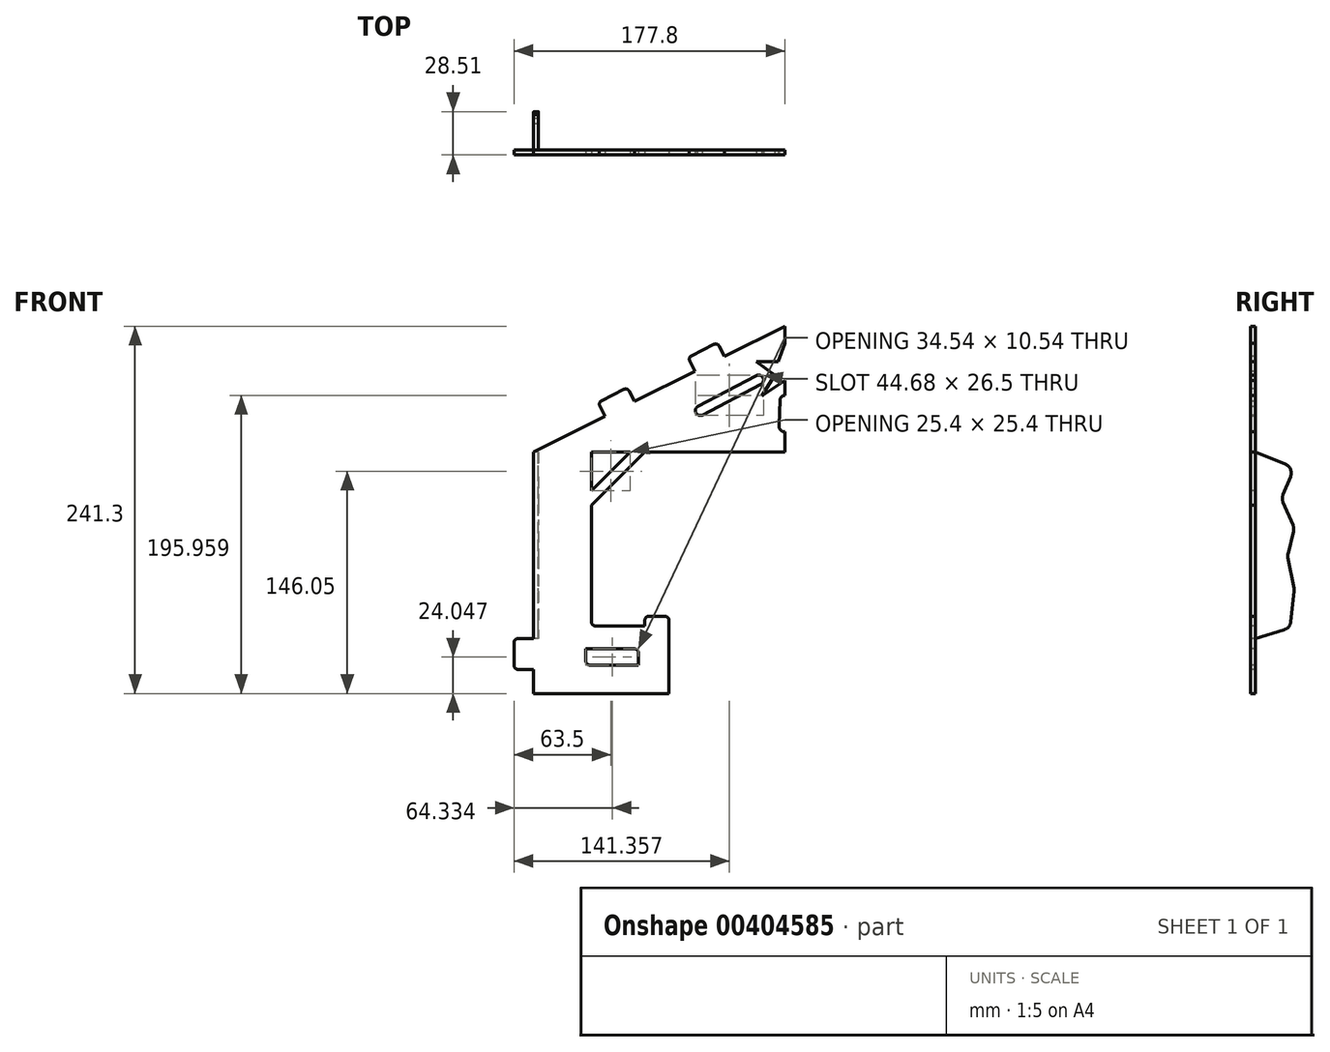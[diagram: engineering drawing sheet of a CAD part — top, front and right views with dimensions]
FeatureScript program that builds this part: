
annotation { "Feature Type Name" : "Feature", "Feature Type Description" : "" }
export const myFeature = defineFeature(function(context is Context, id is Id, definition is map)
    precondition{}
    {
        {
            var Q0;
            Q0=qCreatedBy(makeId("Front.planeOp"),FACE);
            var sketch = newSketch(context, id + "F0", { "sketchPlane" : qUnion([Q0])});
            skLineSegment(sketch, "E0", {"start": v(0, 0) * mm, "end": v(0, 82.55) * mm});
            skLineSegment(sketch, "E1", {"start": v(0, 0) * mm, "end": v(127, 0) * mm});
            skLineSegment(sketch, "E2", {"start": v(127, 0) * mm, "end": v(127, -114.3) * mm});
            skLineSegment(sketch, "E3", {"start": v(127, -114.3) * mm, "end": v(76.2, -114.3) * mm});
            skLineSegment(sketch, "E4", {"start": v(76.2, -114.3) * mm, "end": v(76.2, -158.75) * mm});
            skLineSegment(sketch, "E5", {"start": v(76.2, -158.75) * mm, "end": v(165.1, -158.75) * mm});
            skLineSegment(sketch, "E6", {"start": v(165.1, -158.75) * mm, "end": v(165.1, 0) * mm});
            skPoint(sketch, "E7.orphan", {"position": v(193.1, 0) * mm});
            skLineSegment(sketch, "E8", {"start": v(0, 82.55) * mm, "end": v(165.1, 0) * mm});
            skSolve(sketch);
        }
        {
            var Q0;
            Q0=makeQuery(id+"F0.imprint","IMPRINT",FACE,{"disambiguationData":[TD([[makeQuery(id+"F0.imprint","IMPRINT",EDGE,{"derivedFrom":sQuery(id+"F0.wireOp",EDGE,"E0")}),-1.0]])]});
            extrude(context, id + "F1", {"entities" : qUnion([Q0]), "oppositeDirection" : true, "depth" : 3.17 * mm});
        }
        {
            var Q0;
            Q0=makeQuery(id+"F1.opExtrude","CAP_FACE",FACE,{"disambiguationData":[OSD([sQuery(id+"F0.wireOp",EDGE,"E0"),sQuery(id+"F0.wireOp",EDGE,"E1"),sQuery(id+"F0.wireOp",EDGE,"E2"),sQuery(id+"F0.wireOp",EDGE,"E3"),sQuery(id+"F0.wireOp",EDGE,"E4"),sQuery(id+"F0.wireOp",EDGE,"E5"),sQuery(id+"F0.wireOp",EDGE,"E6"),sQuery(id+"F0.wireOp",EDGE,"E8")])],"isStart":true});
            var sketch = newSketch(context, id + "F2", { "sketchPlane" : qUnion([Q0])});
            skLineSegment(sketch, "E9", {"start": v(39.76, 62.67) * mm, "end": v(44.3, 71.76) * mm});
            skLineSegment(sketch, "E10", {"start": v(44.3, 71.76) * mm, "end": v(63.61, 62.1) * mm});
            skLineSegment(sketch, "E11", {"start": v(63.61, 62.1) * mm, "end": v(59.07, 53.02) * mm});
            skLineSegment(sketch, "E12", {"start": v(59.07, 53.02) * mm, "end": v(39.76, 62.67) * mm});
            skLineSegment(sketch, "E13", {"start": v(78.95, 43.08) * mm, "end": v(85.06, 55.3) * mm, "construction": true});
            skLineSegment(sketch, "E14.MirrorCS", {"start": v(103.37, 42.22) * mm, "end": v(98.83, 33.14) * mm});
            skLineSegment(sketch, "E15.MirrorCS", {"start": v(122.68, 32.57) * mm, "end": v(103.37, 42.22) * mm});
            skLineSegment(sketch, "E16.MirrorCS", {"start": v(118.14, 23.48) * mm, "end": v(122.68, 32.57) * mm});
            skLineSegment(sketch, "E17.MirrorCS", {"start": v(98.83, 33.14) * mm, "end": v(118.14, 23.48) * mm});
            skLineSegment(sketch, "E18.bottom", {"start": v(76.2, -114.3) * mm, "end": v(91.95, -114.3) * mm});
            skLineSegment(sketch, "E18.top", {"start": v(76.2, -107.95) * mm, "end": v(91.95, -107.95) * mm});
            skLineSegment(sketch, "E18.left", {"start": v(76.2, -114.3) * mm, "end": v(76.2, -107.95) * mm});
            skLineSegment(sketch, "E18.right", {"start": v(91.95, -114.3) * mm, "end": v(91.95, -107.95) * mm});
            skLineSegment(sketch, "E19.bottom", {"start": v(165.1, -142.88) * mm, "end": v(177.8, -142.88) * mm});
            skLineSegment(sketch, "E19.top", {"start": v(165.1, -122.55) * mm, "end": v(177.8, -122.55) * mm});
            skLineSegment(sketch, "E19.left", {"start": v(165.1, -142.88) * mm, "end": v(165.1, -122.55) * mm});
            skLineSegment(sketch, "E19.right", {"start": v(177.8, -142.88) * mm, "end": v(177.8, -122.55) * mm});
            skLineSegment(sketch, "E20", {"start": v(101.6, 0) * mm, "end": v(127, -25.4) * mm});
            skLineSegment(sketch, "E21", {"start": v(127, -25.4) * mm, "end": v(127, -34.92) * mm});
            skLineSegment(sketch, "E22", {"start": v(127, -34.92) * mm, "end": v(92.07, 0) * mm});
            skLineSegment(sketch, "E23", {"start": v(92.07, 0) * mm, "end": v(101.6, 0) * mm});
            skSolve(sketch);
        }
        {
            var Q0;
            Q0 = qSketchRegion(id + "F2", true);
            var Q1;
            Q1=makeQuery(id+"F1.opExtrude","CAP_FACE",FACE,{"disambiguationData":[OSD([sQuery(id+"F0.wireOp",EDGE,"E0"),sQuery(id+"F0.wireOp",EDGE,"E1"),sQuery(id+"F0.wireOp",EDGE,"E2"),sQuery(id+"F0.wireOp",EDGE,"E3"),sQuery(id+"F0.wireOp",EDGE,"E4"),sQuery(id+"F0.wireOp",EDGE,"E5"),sQuery(id+"F0.wireOp",EDGE,"E6"),sQuery(id+"F0.wireOp",EDGE,"E8")])],"isStart":false});
            extrude(context, id + "F3", {"entities" : qUnion([Q0]), "operationType" : NewBodyOperationType.ADD, "endBound" : BoundingType.UP_TO_SURFACE, "oppositeDirection" : true, "endBoundEntityFace" : qUnion([Q1]), "depth" : 25.4 * mm});
        }
        {
            var Q0;
            Q0=makeQuery(id+"F3.opExtrude","SWEPT_EDGE",EDGE,{"disambiguationData":[OSD([sQuery(id+"F2.wireOp",EDGE,"E19.bottom"),sQuery(id+"F2.wireOp",EDGE,"E19.right")])]});
            var Q1;
            Q1=makeQuery(id+"F3.opExtrude","SWEPT_EDGE",EDGE,{"disambiguationData":[OSD([sQuery(id+"F2.wireOp",EDGE,"E19.top"),sQuery(id+"F2.wireOp",EDGE,"E19.right")])]});
            var Q2;
            Q2=makeQuery(id+"F3.opExtrude","SWEPT_EDGE",EDGE,{"disambiguationData":[OSD([sQuery(id+"F2.wireOp",EDGE,"E18.top"),sQuery(id+"F2.wireOp",EDGE,"E18.right")])]});
            var Q3;
            Q3=makeQuery(id+"F3.opExtrude","SWEPT_EDGE",EDGE,{"disambiguationData":[OSD([sQuery(id+"F2.wireOp",EDGE,"E15.MirrorCS"),sQuery(id+"F2.wireOp",EDGE,"E16.MirrorCS")])]});
            var Q4;
            Q4=makeQuery(id+"F3.opExtrude","SWEPT_EDGE",EDGE,{"disambiguationData":[OSD([sQuery(id+"F2.wireOp",EDGE,"E10"),sQuery(id+"F2.wireOp",EDGE,"E11")])]});
            var Q5;
            Q5=makeQuery(id+"F3.opExtrude","SWEPT_EDGE",EDGE,{"disambiguationData":[OSD([sQuery(id+"F2.wireOp",EDGE,"E14.MirrorCS"),sQuery(id+"F2.wireOp",EDGE,"E15.MirrorCS")])]});
            var Q6;
            Q6=makeQuery(id+"F3.opExtrude","SWEPT_EDGE",EDGE,{"disambiguationData":[OSD([sQuery(id+"F2.wireOp",EDGE,"E9"),sQuery(id+"F2.wireOp",EDGE,"E10")])]});
            var Q7;
            Q7=makeQuery(id+"F3.opExtrude","SWEPT_EDGE",EDGE,{"disambiguationData":[OSD([sQuery(id+"F2.wireOp",EDGE,"E18.top"),sQuery(id+"F2.wireOp",EDGE,"E18.left")])]});
            var Q8;
            Q8=makeQuery(id+"F3.opExtrude","SWEPT_EDGE",EDGE,{"disambiguationData":[OSD([sQuery(id+"F0.wireOp",EDGE,"E3"),sQuery(id+"F2.wireOp",EDGE,"E18.bottom"),sQuery(id+"F2.wireOp",EDGE,"E18.right")])]});
            var Q9;
            Q9=makeQuery(id+"F1.opExtrude","SWEPT_EDGE",EDGE,{"disambiguationData":[OSD([sQuery(id+"F0.wireOp",EDGE,"E2"),sQuery(id+"F0.wireOp",EDGE,"E3")])]});
            fillet(context, id + "F4", {"entities" : qUnion([Q0, Q1, Q2, Q3, Q4, Q5, Q6, Q7, Q8, Q9]), "radius" : 2.54 * mm, "tangentPropagation" : true, "allowEdgeOverflow" : false});
        }
        {
            var Q0;
            Q0=makeQuery(id+"F3.boolean.opBoolean","MERGE",FACE,{"derivedFrom":[makeQuery(id+"F1.opExtrude","CAP_FACE",FACE,{"disambiguationData":[OSD([sQuery(id+"F0.wireOp",EDGE,"E0"),sQuery(id+"F0.wireOp",EDGE,"E1"),sQuery(id+"F0.wireOp",EDGE,"E2"),sQuery(id+"F0.wireOp",EDGE,"E3"),sQuery(id+"F0.wireOp",EDGE,"E4"),sQuery(id+"F0.wireOp",EDGE,"E5"),sQuery(id+"F0.wireOp",EDGE,"E6"),sQuery(id+"F0.wireOp",EDGE,"E8")])],"isStart":true}),makeQuery(id+"F3.opExtrude","CAP_FACE",FACE,{"disambiguationData":[OSD([sQuery(id+"F2.wireOp",EDGE,"E9"),sQuery(id+"F2.wireOp",EDGE,"E10"),sQuery(id+"F2.wireOp",EDGE,"E11"),sQuery(id+"F2.wireOp",EDGE,"E12")])],"isStart":true}),makeQuery(id+"F3.opExtrude","CAP_FACE",FACE,{"disambiguationData":[OSD([sQuery(id+"F2.wireOp",EDGE,"E14.MirrorCS"),sQuery(id+"F2.wireOp",EDGE,"E15.MirrorCS"),sQuery(id+"F2.wireOp",EDGE,"E16.MirrorCS"),sQuery(id+"F2.wireOp",EDGE,"E17.MirrorCS")])],"isStart":true}),makeQuery(id+"F3.opExtrude","CAP_FACE",FACE,{"disambiguationData":[OSD([sQuery(id+"F2.wireOp",EDGE,"E18.bottom"),sQuery(id+"F2.wireOp",EDGE,"E18.top"),sQuery(id+"F2.wireOp",EDGE,"E18.left"),sQuery(id+"F2.wireOp",EDGE,"E18.right")])],"isStart":true}),makeQuery(id+"F3.opExtrude","CAP_FACE",FACE,{"disambiguationData":[OSD([sQuery(id+"F2.wireOp",EDGE,"E19.bottom"),sQuery(id+"F2.wireOp",EDGE,"E19.top"),sQuery(id+"F2.wireOp",EDGE,"E19.left"),sQuery(id+"F2.wireOp",EDGE,"E19.right")])],"isStart":true}),makeQuery(id+"F3.opExtrude","CAP_FACE",FACE,{"disambiguationData":[OSD([sQuery(id+"F2.wireOp",EDGE,"E20"),sQuery(id+"F2.wireOp",EDGE,"E21"),sQuery(id+"F2.wireOp",EDGE,"E22"),sQuery(id+"F2.wireOp",EDGE,"E23")])],"isStart":true})]});
            var sketch = newSketch(context, id + "F5", { "sketchPlane" : qUnion([Q0])});
            skCircle(sketch, "E24", {"center": v(0, 50.8) * mm, "radius": 20.64 * mm, "construction": true});
            skLineSegment(sketch, "E25", {"start": v(0, 71.44) * mm, "end": v(4.4, 59.14) * mm});
            skLineSegment(sketch, "E26", {"start": v(4.4, 59.14) * mm, "end": v(18.88, 59.14) * mm});
            skLineSegment(sketch, "E27", {"start": v(18.88, 59.14) * mm, "end": v(6.78, 50.36) * mm});
            skLineSegment(sketch, "E28", {"start": v(6.78, 50.36) * mm, "end": v(15.09, 36.72) * mm});
            skLineSegment(sketch, "E29", {"start": v(15.09, 36.72) * mm, "end": v(0, 47.06) * mm});
            skLineSegment(sketch, "E30", {"start": v(0, 71.44) * mm, "end": v(0, 47.06) * mm});
            skArc(sketch, "E31", {"start": v(54.44, 24.19) * mm, "mid": v(58.44, 25.65) * mm, "end": v(57.39, 29.78) * mm});
            skLineSegment(sketch, "E32", {"start": v(18.88, 50.04) * mm, "end": v(18.77, 50.1) * mm});
            skLineSegment(sketch, "E33", {"start": v(54.44, 24.19) * mm, "end": v(15.79, 44.49) * mm});
            skPoint(sketch, "E34.orphan", {"position": v(55.63, 30.3) * mm});
            skLineSegment(sketch, "E35", {"start": v(57.39, 29.78) * mm, "end": v(18.77, 50.1) * mm});
            skArc(sketch, "E36.trimOffspring", {"start": v(18.77, 50.1) * mm, "mid": v(14.46, 48.79) * mm, "end": v(15.79, 44.49) * mm});
            skArc(sketch, "E37", {"start": v(3.17, 34.12) * mm, "mid": v(2.2, 36.27) * mm, "end": v(0, 37.14) * mm});
            skArc(sketch, "E38", {"start": v(0, 13.15) * mm, "mid": v(2.87, 14.37) * mm, "end": v(3.96, 17.3) * mm});
            skLineSegment(sketch, "E39", {"start": v(3.96, 17.3) * mm, "end": v(3.17, 34.12) * mm});
            skLineSegment(sketch, "E40", {"start": v(0, 37.14) * mm, "end": v(0, 13.15) * mm});
            skLineSegment(sketch, "E41.bottom", {"start": v(96.2, -139.97) * mm, "end": v(130.74, -139.97) * mm});
            skLineSegment(sketch, "E41.top", {"start": v(96.2, -129.43) * mm, "end": v(130.74, -129.43) * mm});
            skLineSegment(sketch, "E41.left", {"start": v(96.2, -139.97) * mm, "end": v(96.2, -129.43) * mm});
            skLineSegment(sketch, "E41.right", {"start": v(130.74, -139.97) * mm, "end": v(130.74, -129.43) * mm});
            skSolve(sketch);
        }
        {
            var Q0;
            Q0 = qSketchRegion(id + "F5", true);
            extrude(context, id + "F6", {"entities" : qUnion([Q0]), "operationType" : NewBodyOperationType.REMOVE, "endBound" : BoundingType.THROUGH_ALL, "oppositeDirection" : true, "depth" : 25.4 * mm});
        }
        {
            var Q0;
            {var subQ1=sQuery(id+"F0.wireOp",EDGE,"E8");var subQ2=sQuery(id+"F0.wireOp",EDGE,"E6");Q0=makeQuery(id+"F3.boolean.opBoolean","SPLIT",FACE,{"disambiguationData":[TD([makeQuery(id+"F1.opExtrude","SWEPT_FACE",FACE,{"disambiguationData":[OSD([subQ1])]})])],"derivedFrom":makeQuery(id+"F1.opExtrude","SWEPT_FACE",FACE,{"disambiguationData":[OSD([subQ2])]})});}
            var sketch = newSketch(context, id + "F7", { "sketchPlane" : qUnion([Q0])});
            skLineSegment(sketch, "E42", {"start": v(3.18, 0) * mm, "end": v(28.58, -10.45) * mm});
            skLineSegment(sketch, "E43", {"start": v(28.58, -10.45) * mm, "end": v(20.31, -30.53) * mm});
            skLineSegment(sketch, "E44", {"start": v(20.31, -30.53) * mm, "end": v(28.58, -50.01) * mm});
            skLineSegment(sketch, "E45", {"start": v(28.58, -50.01) * mm, "end": v(24.22, -68.05) * mm});
            skLineSegment(sketch, "E46", {"start": v(24.22, -68.05) * mm, "end": v(28.58, -90.52) * mm});
            skLineSegment(sketch, "E47", {"start": v(28.58, -90.52) * mm, "end": v(25.92, -115.7) * mm});
            skLineSegment(sketch, "E48", {"start": v(25.92, -115.7) * mm, "end": v(3.18, -122.55) * mm});
            skLineSegment(sketch, "E49", {"start": v(3.18, -122.55) * mm, "end": v(3.18, 0) * mm});
            skSolve(sketch);
        }
        {
            var Q0;
            Q0=makeQuery(id+"F7.imprint","IMPRINT",FACE,{"disambiguationData":[TD([[makeQuery(id+"F7.imprint","IMPRINT",EDGE,{"derivedFrom":sQuery(id+"F7.wireOp",EDGE,"E42")}),-1.0]])]});
            extrude(context, id + "F8", {"entities" : qUnion([Q0]), "operationType" : NewBodyOperationType.ADD, "oppositeDirection" : true, "depth" : 3.17 * mm});
        }
        {
            var Q0;
            Q0=makeQuery(id+"F8.opExtrude","SWEPT_EDGE",EDGE,{"disambiguationData":[OSD([sQuery(id+"F7.wireOp",EDGE,"E42"),sQuery(id+"F7.wireOp",EDGE,"E43")])]});
            var Q1;
            Q1=makeQuery(id+"F8.opExtrude","SWEPT_EDGE",EDGE,{"disambiguationData":[OSD([sQuery(id+"F7.wireOp",EDGE,"E43"),sQuery(id+"F7.wireOp",EDGE,"E44")])]});
            var Q2;
            Q2=makeQuery(id+"F8.opExtrude","SWEPT_EDGE",EDGE,{"disambiguationData":[OSD([sQuery(id+"F7.wireOp",EDGE,"E44"),sQuery(id+"F7.wireOp",EDGE,"E45")])]});
            var Q3;
            Q3=makeQuery(id+"F8.opExtrude","SWEPT_EDGE",EDGE,{"disambiguationData":[OSD([sQuery(id+"F7.wireOp",EDGE,"E45"),sQuery(id+"F7.wireOp",EDGE,"E46")])]});
            var Q4;
            Q4=makeQuery(id+"F8.opExtrude","SWEPT_EDGE",EDGE,{"disambiguationData":[OSD([sQuery(id+"F7.wireOp",EDGE,"E46"),sQuery(id+"F7.wireOp",EDGE,"E47")])]});
            var Q5;
            Q5=makeQuery(id+"F8.opExtrude","SWEPT_EDGE",EDGE,{"disambiguationData":[OSD([sQuery(id+"F7.wireOp",EDGE,"E47"),sQuery(id+"F7.wireOp",EDGE,"E48")])]});
            fillet(context, id + "F9", {"entities" : qUnion([Q0, Q1, Q2, Q3, Q4, Q5]), "radius" : 6.35 * mm, "tangentPropagation" : true, "allowEdgeOverflow" : false});
        }
        {
            var Q0;
            Q0=makeQuery(id+"F6.boolean.opBoolean","COPY",EDGE,{"derivedFrom":makeQuery(id+"F6.opExtrude","SWEPT_EDGE",EDGE,{"disambiguationData":[OSD([sQuery(id+"F5.wireOp",EDGE,"E41.top"),sQuery(id+"F5.wireOp",EDGE,"E41.left")])]})});
            var Q1;
            Q1=makeQuery(id+"F6.boolean.opBoolean","COPY",EDGE,{"derivedFrom":makeQuery(id+"F6.opExtrude","SWEPT_EDGE",EDGE,{"disambiguationData":[OSD([sQuery(id+"F5.wireOp",EDGE,"E41.bottom"),sQuery(id+"F5.wireOp",EDGE,"E41.right")])]})});
            fillet(context, id + "F10", {"entities" : qUnion([Q0, Q1]), "radius" : 2.54 * mm, "tangentPropagation" : true, "allowEdgeOverflow" : false});
        }
        {
            var Q0;
            Q0=makeQuery(id+"F1.opExtrude","SWEPT_BODY",BODY,{"disambiguationData":[OSD([sQuery(id+"F0.wireOp",EDGE,"E0"),sQuery(id+"F0.wireOp",EDGE,"E1"),sQuery(id+"F0.wireOp",EDGE,"E2"),sQuery(id+"F0.wireOp",EDGE,"E3"),sQuery(id+"F0.wireOp",EDGE,"E4"),sQuery(id+"F0.wireOp",EDGE,"E5"),sQuery(id+"F0.wireOp",EDGE,"E6"),sQuery(id+"F0.wireOp",EDGE,"E8")])]});
            var Q1;
            Q1=qCreatedBy(makeId("Right.planeOp"),FACE);
            mirror(context, id + "F11", {"operationType" : NewBodyOperationType.ADD, "entities" : qUnion([Q0]), "mirrorPlane" : qUnion([Q1])});
        }
        {
            var Q0;
            Q0=qCreatedBy(makeId("Front.planeOp"),FACE);
            var sketch = newSketch(context, id + "F12", { "sketchPlane" : qUnion([Q0])});
            skLineSegment(sketch, "E50.bottom", {"start": v(0, 100.49) * mm, "end": v(206.84, 100.49) * mm});
            skLineSegment(sketch, "E50.top", {"start": v(0, -168.35) * mm, "end": v(206.84, -168.35) * mm});
            skLineSegment(sketch, "E50.left", {"start": v(0, 100.49) * mm, "end": v(0, -168.35) * mm});
            skLineSegment(sketch, "E50.right", {"start": v(206.84, 100.49) * mm, "end": v(206.84, -168.35) * mm});
            skSolve(sketch);
        }
        {
            var Q0;
            Q0=makeQuery(id+"F12.imprint","IMPRINT",FACE,{"disambiguationData":[TD([[makeQuery(id+"F12.imprint","IMPRINT",EDGE,{"derivedFrom":sQuery(id+"F12.wireOp",EDGE,"E50.bottom")}),-1.0]])]});
            extrude(context, id + "F13", {"entities" : qUnion([Q0]), "operationType" : NewBodyOperationType.REMOVE, "endBound" : BoundingType.THROUGH_ALL, "oppositeDirection" : true, "depth" : 25.4 * mm});
        }
    });
